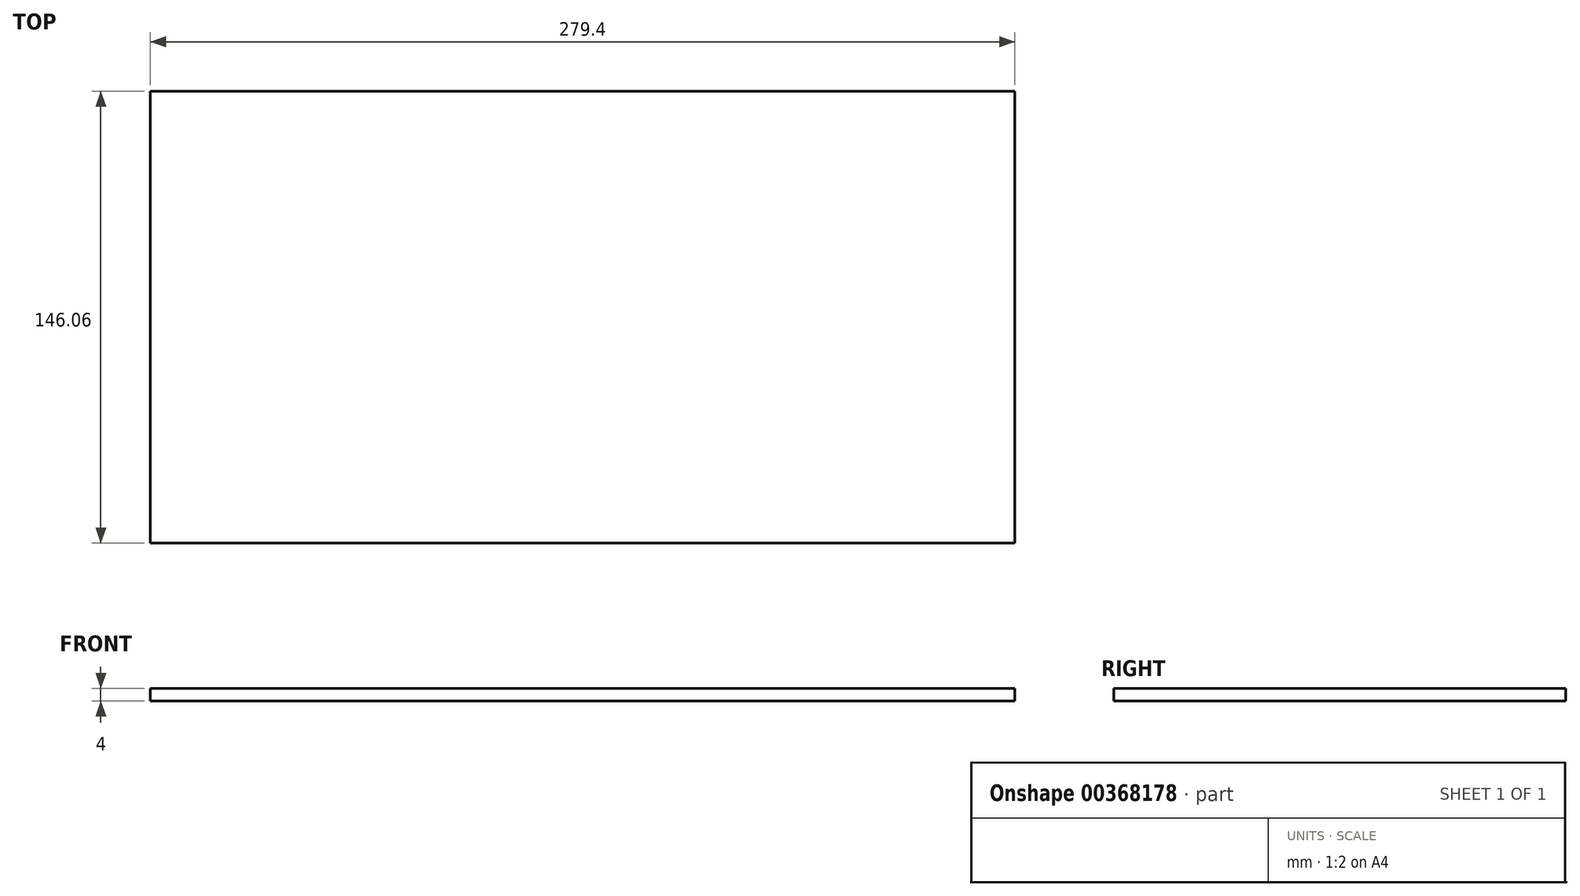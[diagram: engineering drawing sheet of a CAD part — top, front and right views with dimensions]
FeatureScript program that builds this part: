
annotation { "Feature Type Name" : "Feature", "Feature Type Description" : "" }
export const myFeature = defineFeature(function(context is Context, id is Id, definition is map)
    precondition{}
    {
        {
            var Q0;
            Q0=qCreatedBy(makeId("Top.planeOp"),FACE);
            var sketch = newSketch(context, id + "F0", { "sketchPlane" : qUnion([Q0])});
            skLineSegment(sketch, "E0.bottom", {"start": v(139.7, 73.03) * mm, "end": v(-139.7, 73.03) * mm});
            skLineSegment(sketch, "E0.top", {"start": v(139.7, -73.03) * mm, "end": v(-139.7, -73.03) * mm});
            skLineSegment(sketch, "E0.left", {"start": v(139.7, 73.03) * mm, "end": v(139.7, -73.03) * mm});
            skLineSegment(sketch, "E0.right", {"start": v(-139.7, 73.03) * mm, "end": v(-139.7, -73.03) * mm});
            skPoint(sketch, "E0.middle", {"position": v(0, 0) * mm});
            skSolve(sketch);
        }
        {
            var Q0;
            Q0=makeQuery(id+"F0.imprint","IMPRINT",FACE,{"disambiguationData":[TD([[makeQuery(id+"F0.imprint","IMPRINT",EDGE,{"derivedFrom":sQuery(id+"F0.wireOp",EDGE,"E0.bottom")}),1.0]])]});
            extrude(context, id + "F1", {"entities" : qUnion([Q0]), "depth" : 4 * mm});
        }
    });
